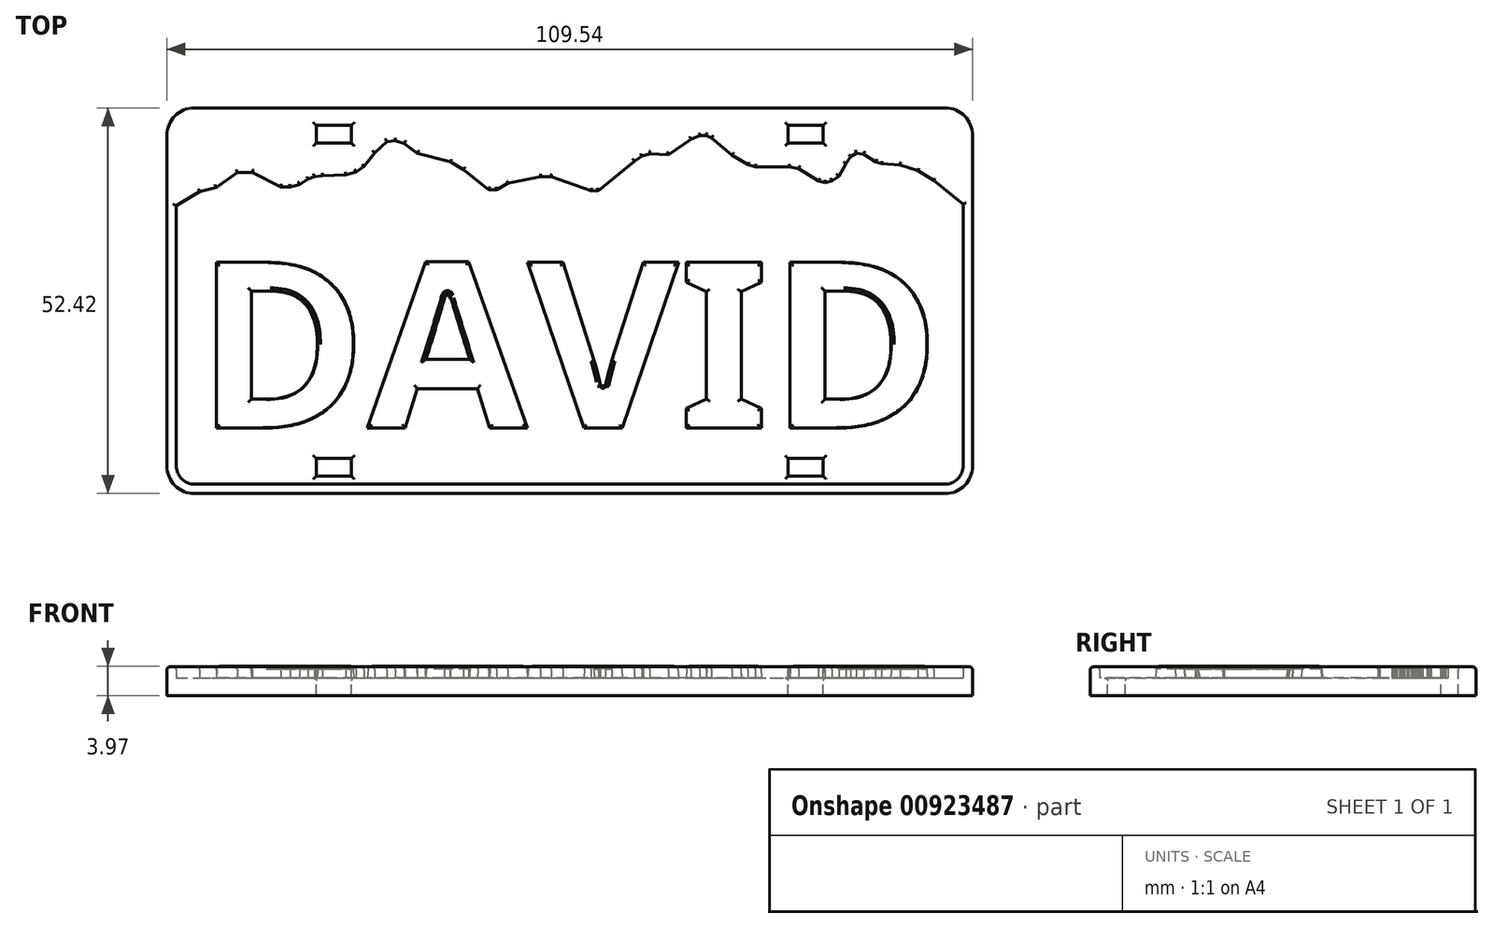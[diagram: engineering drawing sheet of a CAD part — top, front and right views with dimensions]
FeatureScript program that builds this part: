
annotation { "Feature Type Name" : "Feature", "Feature Type Description" : "" }
export const myFeature = defineFeature(function(context is Context, id is Id, definition is map)
    precondition{}
    {
        {
            var Q0;
            Q0=qCreatedBy(makeId("Top.planeOp"),FACE);
            var sketch = newSketch(context, id + "F0", { "sketchPlane" : qUnion([Q0])});
            skLineSegment(sketch, "E0", {"start": v(54.77, -22.46) * mm, "end": v(54.77, 22.46) * mm});
            skArc(sketch, "E1", {"start": v(54.77, 22.46) * mm, "mid": v(53.68, 25.11) * mm, "end": v(51.02, 26.21) * mm});
            skLineSegment(sketch, "E2", {"start": v(51.02, 26.21) * mm, "end": v(-51.02, 26.21) * mm});
            skArc(sketch, "E3", {"start": v(-51.02, 26.21) * mm, "mid": v(-53.68, 25.11) * mm, "end": v(-54.77, 22.46) * mm});
            skLineSegment(sketch, "E4", {"start": v(-54.77, 22.46) * mm, "end": v(-54.77, -22.46) * mm});
            skArc(sketch, "E5", {"start": v(-54.77, -22.46) * mm, "mid": v(-53.54, -25.24) * mm, "end": v(-50.64, -26.2) * mm});
            skLineSegment(sketch, "E6", {"start": v(-50.64, -26.2) * mm, "end": v(51.04, -26.2) * mm});
            skArc(sketch, "E7", {"start": v(51.02, -26.21) * mm, "mid": v(53.68, -25.11) * mm, "end": v(54.77, -22.46) * mm});
            skLineSegment(sketch, "E8", {"start": v(-54.77, 12.13) * mm, "end": v(-50.31, 14.84) * mm});
            skLineSegment(sketch, "E9", {"start": v(-50.31, 14.84) * mm, "end": v(-48.06, 15.4) * mm});
            skLineSegment(sketch, "E10", {"start": v(-48.06, 15.4) * mm, "end": v(-45.2, 17.44) * mm});
            skLineSegment(sketch, "E11", {"start": v(-45.2, 17.44) * mm, "end": v(-43.14, 17.44) * mm});
            skLineSegment(sketch, "E12", {"start": v(-43.14, 17.44) * mm, "end": v(-39.3, 15.5) * mm});
            skLineSegment(sketch, "E13", {"start": v(-39.3, 15.5) * mm, "end": v(-38.03, 15.49) * mm});
            skLineSegment(sketch, "E14", {"start": v(-38.03, 15.49) * mm, "end": v(-36.75, 15.8) * mm});
            skLineSegment(sketch, "E15", {"start": v(-36.75, 15.8) * mm, "end": v(-35.57, 16.54) * mm});
            skLineSegment(sketch, "E16", {"start": v(-35.57, 16.54) * mm, "end": v(-34.73, 16.88) * mm});
            skLineSegment(sketch, "E17", {"start": v(-34.73, 16.88) * mm, "end": v(-33.6, 17.01) * mm});
            skLineSegment(sketch, "E18", {"start": v(-33.6, 17.01) * mm, "end": v(-30.43, 17.11) * mm});
            skLineSegment(sketch, "E19", {"start": v(-29.05, 17.5) * mm, "end": v(-27.98, 18.27) * mm});
            skLineSegment(sketch, "E20", {"start": v(-27.98, 18.27) * mm, "end": v(-26.53, 20.14) * mm});
            skLineSegment(sketch, "E21", {"start": v(-26.53, 20.14) * mm, "end": v(-24.88, 21.63) * mm});
            skLineSegment(sketch, "E22", {"start": v(-24.88, 21.63) * mm, "end": v(-23.73, 21.77) * mm});
            skLineSegment(sketch, "E23", {"start": v(-22.5, 21.4) * mm, "end": v(-20.72, 20.04) * mm});
            skLineSegment(sketch, "E24", {"start": v(-16.23, 18.87) * mm, "end": v(-14.45, 17.85) * mm});
            skLineSegment(sketch, "E25", {"start": v(-14.45, 17.85) * mm, "end": v(-11.02, 15.1) * mm});
            skLineSegment(sketch, "E26", {"start": v(-11.02, 15.1) * mm, "end": v(-9.93, 15.1) * mm});
            skLineSegment(sketch, "E27", {"start": v(-9.93, 15.1) * mm, "end": v(-8.4, 15.96) * mm});
            skLineSegment(sketch, "E28", {"start": v(-8.4, 15.96) * mm, "end": v(-3.94, 16.85) * mm});
            skLineSegment(sketch, "E29", {"start": v(-3.94, 16.85) * mm, "end": v(-2.54, 16.85) * mm});
            skLineSegment(sketch, "E30", {"start": v(-2.54, 16.85) * mm, "end": v(2.9, 14.97) * mm});
            skLineSegment(sketch, "E31", {"start": v(2.9, 14.97) * mm, "end": v(3.92, 14.97) * mm});
            skLineSegment(sketch, "E32", {"start": v(3.92, 14.97) * mm, "end": v(8.8, 18.97) * mm});
            skLineSegment(sketch, "E33", {"start": v(8.8, 18.97) * mm, "end": v(9.82, 19.64) * mm});
            skLineSegment(sketch, "E34", {"start": v(9.82, 19.64) * mm, "end": v(10.9, 19.97) * mm});
            skLineSegment(sketch, "E35", {"start": v(10.9, 19.97) * mm, "end": v(13.43, 19.86) * mm});
            skLineSegment(sketch, "E36", {"start": v(16.5, 21.96) * mm, "end": v(17.71, 22.42) * mm});
            skLineSegment(sketch, "E37", {"start": v(17.71, 22.42) * mm, "end": v(18.56, 22.45) * mm});
            skLineSegment(sketch, "E38", {"start": v(18.56, 22.45) * mm, "end": v(19.28, 22.13) * mm});
            skLineSegment(sketch, "E39", {"start": v(19.28, 22.13) * mm, "end": v(22.05, 19.8) * mm});
            skLineSegment(sketch, "E40", {"start": v(22.05, 19.8) * mm, "end": v(24.2, 18.5) * mm});
            skLineSegment(sketch, "E41", {"start": v(24.2, 18.5) * mm, "end": v(25.23, 18.2) * mm});
            skLineSegment(sketch, "E42", {"start": v(25.23, 18.2) * mm, "end": v(29.85, 18.2) * mm});
            skLineSegment(sketch, "E43", {"start": v(29.85, 18.2) * mm, "end": v(31.13, 17.95) * mm});
            skLineSegment(sketch, "E44", {"start": v(31.13, 17.95) * mm, "end": v(33.84, 16.27) * mm});
            skLineSegment(sketch, "E45", {"start": v(33.84, 16.27) * mm, "end": v(34.73, 16.06) * mm});
            skLineSegment(sketch, "E46", {"start": v(34.73, 16.06) * mm, "end": v(35.67, 16.3) * mm});
            skLineSegment(sketch, "E47", {"start": v(35.67, 16.3) * mm, "end": v(36.58, 16.95) * mm});
            skLineSegment(sketch, "E48", {"start": v(36.58, 16.95) * mm, "end": v(37.58, 18.67) * mm});
            skLineSegment(sketch, "E49", {"start": v(38.22, 19.58) * mm, "end": v(38.96, 20.06) * mm});
            skLineSegment(sketch, "E50", {"start": v(38.96, 20.06) * mm, "end": v(39.94, 19.92) * mm});
            skLineSegment(sketch, "E51", {"start": v(41.58, 18.88) * mm, "end": v(42.4, 18.61) * mm});
            skLineSegment(sketch, "E52", {"start": v(42.4, 18.61) * mm, "end": v(44.9, 18.47) * mm});
            skLineSegment(sketch, "E53", {"start": v(44.9, 18.47) * mm, "end": v(47.31, 17.68) * mm});
            skLineSegment(sketch, "E54", {"start": v(47.31, 17.68) * mm, "end": v(49.47, 16.33) * mm});
            skLineSegment(sketch, "E55", {"start": v(49.47, 16.33) * mm, "end": v(51.88, 14.42) * mm});
            skLineSegment(sketch, "E56", {"start": v(51.88, 14.42) * mm, "end": v(53.78, 12.92) * mm});
            skLineSegment(sketch, "E57", {"start": v(53.78, 12.92) * mm, "end": v(54.77, 12.06) * mm});
            skLineSegment(sketch, "E58", {"start": v(-20.72, 20.04) * mm, "end": v(-16.23, 18.87) * mm});
            skLineSegment(sketch, "E59", {"start": v(16.5, 21.96) * mm, "end": v(13.43, 19.86) * mm});
            skLineSegment(sketch, "E60", {"start": v(-22.5, 21.4) * mm, "end": v(-23.73, 21.77) * mm});
            skLineSegment(sketch, "E61", {"start": v(-29.05, 17.5) * mm, "end": v(-30.43, 17.11) * mm});
            skLineSegment(sketch, "E62", {"start": v(37.58, 18.67) * mm, "end": v(38.22, 19.58) * mm});
            skLineSegment(sketch, "E63", {"start": v(41.58, 18.88) * mm, "end": v(39.94, 19.92) * mm});
            skSolve(sketch);
        }
        {
            var Q0;
            Q0=qCreatedBy(makeId("Top.planeOp"),FACE);
            var sketch = newSketch(context, id + "F1", { "sketchPlane" : qUnion([Q0])});
            skLineSegment(sketch, "E64", {"start": v(54.77, -22.46) * mm, "end": v(54.77, 22.46) * mm});
            skArc(sketch, "E65", {"start": v(54.77, 22.46) * mm, "mid": v(53.68, 25.11) * mm, "end": v(51.02, 26.21) * mm});
            skLineSegment(sketch, "E66", {"start": v(51.02, 26.21) * mm, "end": v(-51.02, 26.21) * mm});
            skArc(sketch, "E67", {"start": v(-51.02, 26.21) * mm, "mid": v(-53.68, 25.11) * mm, "end": v(-54.77, 22.46) * mm});
            skLineSegment(sketch, "E68", {"start": v(-54.77, 22.46) * mm, "end": v(-54.77, -22.46) * mm});
            skArc(sketch, "E69", {"start": v(-54.77, -22.46) * mm, "mid": v(-53.68, -25.11) * mm, "end": v(-51.02, -26.21) * mm});
            skLineSegment(sketch, "E70", {"start": v(-51.02, -26.21) * mm, "end": v(51.02, -26.21) * mm});
            skArc(sketch, "E71", {"start": v(51.02, -26.21) * mm, "mid": v(53.68, -25.11) * mm, "end": v(54.77, -22.46) * mm});
            skLineSegment(sketch, "E72.0", {"start": v(50.96, 24.94) * mm, "end": v(-50.96, 24.94) * mm, "construction": true});
            skLineSegment(sketch, "E72.1", {"start": v(53.5, -22.4) * mm, "end": v(53.5, 22.4) * mm, "construction": true});
            skLineSegment(sketch, "E72.2", {"start": v(-50.96, -24.94) * mm, "end": v(50.96, -24.94) * mm, "construction": true});
            skLineSegment(sketch, "E72.3", {"start": v(-53.5, 22.4) * mm, "end": v(-53.5, -22.4) * mm, "construction": true});
            skPoint(sketch, "E73.visualSharp", {"position": v(-53.5, 24.94) * mm});
            skArc(sketch, "E73.filletArc", {"start": v(-50.96, 24.94) * mm, "mid": v(-52.76, 24.2) * mm, "end": v(-53.5, 22.4) * mm, "construction": true});
            skPoint(sketch, "E74.visualSharp", {"position": v(-53.5, -24.94) * mm});
            skArc(sketch, "E74.filletArc", {"start": v(-53.5, -22.4) * mm, "mid": v(-52.76, -24.2) * mm, "end": v(-50.96, -24.94) * mm, "construction": true});
            skPoint(sketch, "E75.visualSharp", {"position": v(53.5, -24.94) * mm});
            skArc(sketch, "E75.filletArc", {"start": v(50.96, -24.94) * mm, "mid": v(52.76, -24.2) * mm, "end": v(53.5, -22.4) * mm, "construction": true});
            skPoint(sketch, "E76.visualSharp", {"position": v(53.5, 24.94) * mm});
            skArc(sketch, "E76.filletArc", {"start": v(53.5, 22.4) * mm, "mid": v(52.76, 24.2) * mm, "end": v(50.96, 24.94) * mm, "construction": true});
            skSolve(sketch);
        }
        {
            var Q0;
            {var subQ3=sQuery(id+"F0.wireOp",EDGE,"E1");Q0=makeQuery(id+"F0.imprint","IMPRINT",FACE,{"disambiguationData":[TD([[makeQuery(id+"F0.imprint","IMPRINT",EDGE,{"derivedFrom":subQ3}),1.0]])]});}
            extrude(context, id + "F2", {"entities" : qUnion([Q0]), "depth" : 1.52 * mm, "offsetDistance" : 25.4 * mm});
        }
        {
            var Q0;
            Q0=qSketchRegion(id+"F1",true);
            extrude(context, id + "F3", {"entities" : qUnion([Q0]), "operationType" : NewBodyOperationType.ADD, "oppositeDirection" : true, "depth" : 2.38 * mm, "offsetDistance" : 25.4 * mm});
        }
        {
            var Q0;
            {var subQ58=sQuery(id+"F0.wireOp",EDGE,"E0");var subQ59=sQuery(id+"F1.wireOp",EDGE,"E64");var subQ60=sQuery(id+"F1.wireOp",EDGE,"E65");var subQ61=sQuery(id+"F1.wireOp",EDGE,"E68");var subQ62=sQuery(id+"F1.wireOp",EDGE,"E69");var subQ63=sQuery(id+"F1.wireOp",EDGE,"E70");var subQ64=sQuery(id+"F1.wireOp",EDGE,"E71");Q0=makeQuery(id+"F3.boolean.opBoolean","SPLIT",FACE,{"disambiguationData":[TD([makeQuery(id+"F2.opExtrude","SWEPT_FACE",FACE,{"disambiguationData":[OSD([subQ58])]})])],"derivedFrom":makeQuery(id+"F3.opExtrude","CAP_FACE",FACE,{"disambiguationData":[OSD([subQ59,subQ60,sQuery(id+"F1.wireOp",EDGE,"E66"),sQuery(id+"F1.wireOp",EDGE,"E67"),subQ61,subQ62,subQ63,subQ64])],"isStart":true})});}
            var sketch = newSketch(context, id + "F4", { "sketchPlane" : qUnion([Q0])});
            skLineSegment(sketch, "E77", {"start": v(54.77, -22.46) * mm, "end": v(54.77, 12.06) * mm});
            skLineSegment(sketch, "E78", {"start": v(-54.77, 12.13) * mm, "end": v(-54.77, -22.46) * mm});
            skArc(sketch, "E79", {"start": v(-54.77, -22.46) * mm, "mid": v(-53.68, -25.11) * mm, "end": v(-51.02, -26.21) * mm});
            skLineSegment(sketch, "E80", {"start": v(-51.02, -26.21) * mm, "end": v(51.02, -26.21) * mm});
            skArc(sketch, "E81", {"start": v(51.02, -26.21) * mm, "mid": v(53.68, -25.11) * mm, "end": v(54.77, -22.46) * mm});
            skLineSegment(sketch, "E82.1", {"start": v(53.5, -22.4) * mm, "end": v(53.5, 13.14) * mm});
            skLineSegment(sketch, "E82.2", {"start": v(-50.96, -24.94) * mm, "end": v(50.96, -24.94) * mm});
            skLineSegment(sketch, "E82.3", {"start": v(-53.5, 12.9) * mm, "end": v(-53.5, -22.4) * mm});
            skPoint(sketch, "E83.visualSharp", {"position": v(-53.5, 24.94) * mm});
            skPoint(sketch, "E84.visualSharp", {"position": v(-53.5, -24.94) * mm});
            skArc(sketch, "E84.filletArc", {"start": v(-53.5, -22.4) * mm, "mid": v(-52.76, -24.2) * mm, "end": v(-50.96, -24.94) * mm});
            skPoint(sketch, "E85.visualSharp", {"position": v(53.5, -24.94) * mm});
            skArc(sketch, "E85.filletArc", {"start": v(50.96, -24.94) * mm, "mid": v(52.76, -24.2) * mm, "end": v(53.5, -22.4) * mm});
            skPoint(sketch, "E86.visualSharp", {"position": v(53.5, 24.94) * mm});
            skLineSegment(sketch, "E87", {"start": v(-54.77, 12.13) * mm, "end": v(-53.5, 12.9) * mm});
            skLineSegment(sketch, "E88", {"start": v(53.5, 13.14) * mm, "end": v(53.78, 12.92) * mm});
            skLineSegment(sketch, "E89", {"start": v(53.78, 12.92) * mm, "end": v(54.77, 12.06) * mm});
            skSolve(sketch);
        }
        {
            var Q0;
            Q0=qSketchRegion(id+"F4",true);
            extrude(context, id + "F5", {"entities" : qUnion([Q0]), "operationType" : NewBodyOperationType.ADD, "depth" : 1.52 * mm, "offsetDistance" : 25.4 * mm});
        }
        {
            var Q0;
            Q0=makeQuery(id+"F5.boolean.opBoolean","MERGE",FACE,{"derivedFrom":[makeQuery(id+"F2.opExtrude","CAP_FACE",FACE,{"disambiguationData":[OSD([sQuery(id+"F0.wireOp",EDGE,"E0"),sQuery(id+"F0.wireOp",EDGE,"E1"),sQuery(id+"F0.wireOp",EDGE,"E2"),sQuery(id+"F0.wireOp",EDGE,"E3"),sQuery(id+"F0.wireOp",EDGE,"E4"),sQuery(id+"F0.wireOp",EDGE,"E8"),sQuery(id+"F0.wireOp",EDGE,"E9"),sQuery(id+"F0.wireOp",EDGE,"E10"),sQuery(id+"F0.wireOp",EDGE,"E11"),sQuery(id+"F0.wireOp",EDGE,"E12"),sQuery(id+"F0.wireOp",EDGE,"E13"),sQuery(id+"F0.wireOp",EDGE,"E14"),sQuery(id+"F0.wireOp",EDGE,"E15"),sQuery(id+"F0.wireOp",EDGE,"E16"),sQuery(id+"F0.wireOp",EDGE,"E17"),sQuery(id+"F0.wireOp",EDGE,"E18"),sQuery(id+"F0.wireOp",EDGE,"7b9f405e-0691-426e-9c9e-a5372cf0836a"),sQuery(id+"F0.wireOp",EDGE,"E19"),sQuery(id+"F0.wireOp",EDGE,"E20"),sQuery(id+"F0.wireOp",EDGE,"E21"),sQuery(id+"F0.wireOp",EDGE,"E22"),sQuery(id+"F0.wireOp",EDGE,"b3dec5b1-662c-4d50-a13c-af7b7760114a"),sQuery(id+"F0.wireOp",EDGE,"E23"),sQuery(id+"F0.wireOp",EDGE,"4d9ee76e-0833-4cdc-b1a8-2d4ce76e6521"),sQuery(id+"F0.wireOp",EDGE,"E24"),sQuery(id+"F0.wireOp",EDGE,"E25"),sQuery(id+"F0.wireOp",EDGE,"E26"),sQuery(id+"F0.wireOp",EDGE,"E27"),sQuery(id+"F0.wireOp",EDGE,"E28"),sQuery(id+"F0.wireOp",EDGE,"E29"),sQuery(id+"F0.wireOp",EDGE,"E30"),sQuery(id+"F0.wireOp",EDGE,"E31"),sQuery(id+"F0.wireOp",EDGE,"E32"),sQuery(id+"F0.wireOp",EDGE,"E33"),sQuery(id+"F0.wireOp",EDGE,"E34"),sQuery(id+"F0.wireOp",EDGE,"E35"),sQuery(id+"F0.wireOp",EDGE,"55551997-bb9e-4b94-90c5-def3cb147476"),sQuery(id+"F0.wireOp",EDGE,"E36"),sQuery(id+"F0.wireOp",EDGE,"E37"),sQuery(id+"F0.wireOp",EDGE,"E38"),sQuery(id+"F0.wireOp",EDGE,"E39"),sQuery(id+"F0.wireOp",EDGE,"E40"),sQuery(id+"F0.wireOp",EDGE,"E41"),sQuery(id+"F0.wireOp",EDGE,"E42"),sQuery(id+"F0.wireOp",EDGE,"E43"),sQuery(id+"F0.wireOp",EDGE,"E44"),sQuery(id+"F0.wireOp",EDGE,"E45"),sQuery(id+"F0.wireOp",EDGE,"E46"),sQuery(id+"F0.wireOp",EDGE,"E47"),sQuery(id+"F0.wireOp",EDGE,"E48"),sQuery(id+"F0.wireOp",EDGE,"513b7cbe-d979-4e22-b277-f3c42ccdbda1"),sQuery(id+"F0.wireOp",EDGE,"E49"),sQuery(id+"F0.wireOp",EDGE,"E50"),sQuery(id+"F0.wireOp",EDGE,"0d842e13-672c-40e3-aae4-28923e78d4e0"),sQuery(id+"F0.wireOp",EDGE,"E51"),sQuery(id+"F0.wireOp",EDGE,"E52"),sQuery(id+"F0.wireOp",EDGE,"E53"),sQuery(id+"F0.wireOp",EDGE,"E54"),sQuery(id+"F0.wireOp",EDGE,"E55"),sQuery(id+"F0.wireOp",EDGE,"E56"),sQuery(id+"F0.wireOp",EDGE,"E57")])],"isStart":false}),makeQuery(id+"F5.opExtrude","CAP_FACE",FACE,{"disambiguationData":[OSD([sQuery(id+"F4.wireOp",EDGE,"E77"),sQuery(id+"F4.wireOp",EDGE,"E78"),sQuery(id+"F4.wireOp",EDGE,"E79"),sQuery(id+"F4.wireOp",EDGE,"E80"),sQuery(id+"F4.wireOp",EDGE,"E81"),sQuery(id+"F4.wireOp",EDGE,"E82.1"),sQuery(id+"F4.wireOp",EDGE,"E82.2"),sQuery(id+"F4.wireOp",EDGE,"E82.3"),sQuery(id+"F4.wireOp",EDGE,"E84.filletArc"),sQuery(id+"F4.wireOp",EDGE,"E85.filletArc"),sQuery(id+"F4.wireOp",EDGE,"E87"),sQuery(id+"F4.wireOp",EDGE,"E88"),sQuery(id+"F4.wireOp",EDGE,"E89")])],"isStart":false})]});
            var sketch = newSketch(context, id + "F6", { "sketchPlane" : qUnion([Q0])});
            skLineSegment(sketch, "E90.bottom", {"start": v(-34.45, 23.83) * mm, "end": v(-29.7, 23.83) * mm});
            skLineSegment(sketch, "E90.top", {"start": v(-34.45, 21.45) * mm, "end": v(-29.7, 21.45) * mm});
            skLineSegment(sketch, "E90.left", {"start": v(-34.45, 23.83) * mm, "end": v(-34.45, 21.45) * mm});
            skLineSegment(sketch, "E90.right", {"start": v(-29.7, 23.83) * mm, "end": v(-29.7, 21.45) * mm});
            skLineSegment(sketch, "E91", {"start": v(0, 26.21) * mm, "end": v(0, -26.21) * mm, "construction": true});
            skLineSegment(sketch, "E92.MirrorCS", {"start": v(34.45, 23.83) * mm, "end": v(34.45, 21.45) * mm});
            skLineSegment(sketch, "E93.MirrorCS", {"start": v(29.7, 23.83) * mm, "end": v(29.7, 21.45) * mm});
            skLineSegment(sketch, "E94.MirrorCS", {"start": v(34.45, 21.45) * mm, "end": v(29.7, 21.45) * mm});
            skLineSegment(sketch, "E95.MirrorCS", {"start": v(34.45, 23.83) * mm, "end": v(29.7, 23.83) * mm});
            skLineSegment(sketch, "E96", {"start": v(0, 0) * mm, "end": v(-59.23, 0) * mm, "construction": true});
            skLineSegment(sketch, "E97", {"start": v(0, 0) * mm, "end": v(56.47, 0) * mm, "construction": true});
            skLineSegment(sketch, "E98.MirrorCS", {"start": v(-34.45, -23.83) * mm, "end": v(-29.7, -23.83) * mm});
            skLineSegment(sketch, "E99.MirrorCS", {"start": v(-34.45, -23.83) * mm, "end": v(-34.45, -21.45) * mm});
            skLineSegment(sketch, "E100.MirrorCS", {"start": v(-34.45, -21.45) * mm, "end": v(-29.7, -21.45) * mm});
            skLineSegment(sketch, "E101.MirrorCS", {"start": v(-29.7, -23.83) * mm, "end": v(-29.7, -21.45) * mm});
            skLineSegment(sketch, "E102.MirrorCS", {"start": v(29.7, -23.83) * mm, "end": v(29.7, -21.45) * mm});
            skLineSegment(sketch, "E103.MirrorCS", {"start": v(34.45, -23.83) * mm, "end": v(29.7, -23.83) * mm});
            skLineSegment(sketch, "E104.MirrorCS", {"start": v(34.45, -23.83) * mm, "end": v(34.45, -21.45) * mm});
            skLineSegment(sketch, "E105.MirrorCS", {"start": v(34.45, -21.45) * mm, "end": v(29.7, -21.45) * mm});
            skSolve(sketch);
        }
        {
            var Q0;
            Q0=qSketchRegion(id+"F6",true);
            extrude(context, id + "F7", {"entities" : qUnion([Q0]), "operationType" : NewBodyOperationType.REMOVE, "endBound" : BoundingType.THROUGH_ALL, "oppositeDirection" : true, "depth" : 25.4 * mm, "offsetDistance" : 25.4 * mm});
        }
        {
            var Q0;
            Q0=makeQuery(id+"F3.opExtrude","CAP_FACE",FACE,{"disambiguationData":[OSD([sQuery(id+"F1.wireOp",EDGE,"E64"),sQuery(id+"F1.wireOp",EDGE,"E65"),sQuery(id+"F1.wireOp",EDGE,"E66"),sQuery(id+"F1.wireOp",EDGE,"E67"),sQuery(id+"F1.wireOp",EDGE,"E68"),sQuery(id+"F1.wireOp",EDGE,"E69"),sQuery(id+"F1.wireOp",EDGE,"E70"),sQuery(id+"F1.wireOp",EDGE,"E71")])],"isStart":true});
            var sketch = newSketch(context, id + "F8", { "sketchPlane" : qUnion([Q0])});
            skText(sketch, "E106", { "text": "DAVID", "fontName": "NotoSans-Bold.ttf"});
            const initialGuessF8  = {"E106": [-0.0509, -0.01732, 1, 0, 0.02274]};
            skSetInitialGuess(sketch, initialGuessF8);
            skSolve(sketch);
        }
        {
            var Q0;
            Q0=qSketchRegion(id+"F8",true);
            extrude(context, id + "F9", {"entities" : qUnion([Q0]), "operationType" : NewBodyOperationType.ADD, "depth" : 1.59 * mm, "offsetDistance" : 25.4 * mm, "hasDraft" : true, "draftAngle" : 3 * degree, "draftPullDirection" : true});
        }
        {
            var Q0;
            Q0=makeQuery(id+"F5.boolean.opBoolean","MERGE",FACE,{"derivedFrom":[makeQuery(id+"F2.opExtrude","CAP_FACE",FACE,{"disambiguationData":[OSD([sQuery(id+"F0.wireOp",EDGE,"E0"),sQuery(id+"F0.wireOp",EDGE,"E1"),sQuery(id+"F0.wireOp",EDGE,"E2"),sQuery(id+"F0.wireOp",EDGE,"E3"),sQuery(id+"F0.wireOp",EDGE,"E4"),sQuery(id+"F0.wireOp",EDGE,"E8"),sQuery(id+"F0.wireOp",EDGE,"E9"),sQuery(id+"F0.wireOp",EDGE,"E10"),sQuery(id+"F0.wireOp",EDGE,"E11"),sQuery(id+"F0.wireOp",EDGE,"E12"),sQuery(id+"F0.wireOp",EDGE,"E13"),sQuery(id+"F0.wireOp",EDGE,"E14"),sQuery(id+"F0.wireOp",EDGE,"E15"),sQuery(id+"F0.wireOp",EDGE,"E16"),sQuery(id+"F0.wireOp",EDGE,"E17"),sQuery(id+"F0.wireOp",EDGE,"E18"),sQuery(id+"F0.wireOp",EDGE,"7b9f405e-0691-426e-9c9e-a5372cf0836a"),sQuery(id+"F0.wireOp",EDGE,"E19"),sQuery(id+"F0.wireOp",EDGE,"E20"),sQuery(id+"F0.wireOp",EDGE,"E21"),sQuery(id+"F0.wireOp",EDGE,"E22"),sQuery(id+"F0.wireOp",EDGE,"b3dec5b1-662c-4d50-a13c-af7b7760114a"),sQuery(id+"F0.wireOp",EDGE,"E23"),sQuery(id+"F0.wireOp",EDGE,"4d9ee76e-0833-4cdc-b1a8-2d4ce76e6521"),sQuery(id+"F0.wireOp",EDGE,"E24"),sQuery(id+"F0.wireOp",EDGE,"E25"),sQuery(id+"F0.wireOp",EDGE,"E26"),sQuery(id+"F0.wireOp",EDGE,"E27"),sQuery(id+"F0.wireOp",EDGE,"E28"),sQuery(id+"F0.wireOp",EDGE,"E29"),sQuery(id+"F0.wireOp",EDGE,"E30"),sQuery(id+"F0.wireOp",EDGE,"E31"),sQuery(id+"F0.wireOp",EDGE,"E32"),sQuery(id+"F0.wireOp",EDGE,"E33"),sQuery(id+"F0.wireOp",EDGE,"E34"),sQuery(id+"F0.wireOp",EDGE,"E35"),sQuery(id+"F0.wireOp",EDGE,"55551997-bb9e-4b94-90c5-def3cb147476"),sQuery(id+"F0.wireOp",EDGE,"E36"),sQuery(id+"F0.wireOp",EDGE,"E37"),sQuery(id+"F0.wireOp",EDGE,"E38"),sQuery(id+"F0.wireOp",EDGE,"E39"),sQuery(id+"F0.wireOp",EDGE,"E40"),sQuery(id+"F0.wireOp",EDGE,"E41"),sQuery(id+"F0.wireOp",EDGE,"E42"),sQuery(id+"F0.wireOp",EDGE,"E43"),sQuery(id+"F0.wireOp",EDGE,"E44"),sQuery(id+"F0.wireOp",EDGE,"E45"),sQuery(id+"F0.wireOp",EDGE,"E46"),sQuery(id+"F0.wireOp",EDGE,"E47"),sQuery(id+"F0.wireOp",EDGE,"E48"),sQuery(id+"F0.wireOp",EDGE,"513b7cbe-d979-4e22-b277-f3c42ccdbda1"),sQuery(id+"F0.wireOp",EDGE,"E49"),sQuery(id+"F0.wireOp",EDGE,"E50"),sQuery(id+"F0.wireOp",EDGE,"0d842e13-672c-40e3-aae4-28923e78d4e0"),sQuery(id+"F0.wireOp",EDGE,"E51"),sQuery(id+"F0.wireOp",EDGE,"E52"),sQuery(id+"F0.wireOp",EDGE,"E53"),sQuery(id+"F0.wireOp",EDGE,"E54"),sQuery(id+"F0.wireOp",EDGE,"E55"),sQuery(id+"F0.wireOp",EDGE,"E56"),sQuery(id+"F0.wireOp",EDGE,"E57")])],"isStart":false}),makeQuery(id+"F5.opExtrude","CAP_FACE",FACE,{"disambiguationData":[OSD([sQuery(id+"F4.wireOp",EDGE,"E77"),sQuery(id+"F4.wireOp",EDGE,"E78"),sQuery(id+"F4.wireOp",EDGE,"E79"),sQuery(id+"F4.wireOp",EDGE,"E80"),sQuery(id+"F4.wireOp",EDGE,"E81"),sQuery(id+"F4.wireOp",EDGE,"E82.1"),sQuery(id+"F4.wireOp",EDGE,"E82.2"),sQuery(id+"F4.wireOp",EDGE,"E82.3"),sQuery(id+"F4.wireOp",EDGE,"E84.filletArc"),sQuery(id+"F4.wireOp",EDGE,"E85.filletArc"),sQuery(id+"F4.wireOp",EDGE,"E87"),sQuery(id+"F4.wireOp",EDGE,"E88"),sQuery(id+"F4.wireOp",EDGE,"E89")])],"isStart":false})]});
            var Q1;
            {var subQ0=sQuery(id+"F1.wireOp",EDGE,"E64");var subQ1=sQuery(id+"F1.wireOp",EDGE,"E68");var subQ2=sQuery(id+"F1.wireOp",EDGE,"E69");var subQ3=sQuery(id+"F1.wireOp",EDGE,"E70");var subQ4=sQuery(id+"F1.wireOp",EDGE,"E71");Q1=makeQuery(id+"F7.boolean.opBoolean","INTERSECT",EDGE,{"derivedFrom":[makeQuery(id+"F3.boolean.opBoolean","SPLIT",FACE,{"disambiguationData":[TD([makeQuery(id+"F2.opExtrude","SWEPT_FACE",FACE,{"disambiguationData":[OSD([sQuery(id+"F0.wireOp",EDGE,"E0")])]})])],"derivedFrom":makeQuery(id+"F3.opExtrude","CAP_FACE",FACE,{"disambiguationData":[OSD([subQ0,sQuery(id+"F1.wireOp",EDGE,"E65"),sQuery(id+"F1.wireOp",EDGE,"E66"),sQuery(id+"F1.wireOp",EDGE,"E67"),subQ1,subQ2,subQ3,subQ4])],"isStart":true})}),makeQuery(id+"F7.opExtrude","SWEPT_FACE",FACE,{"disambiguationData":[OSD([sQuery(id+"F6.wireOp",EDGE,"E100.MirrorCS")])]})]});}
            var Q2;
            {var subQ0=sQuery(id+"F1.wireOp",EDGE,"E64");var subQ1=sQuery(id+"F1.wireOp",EDGE,"E68");var subQ2=sQuery(id+"F1.wireOp",EDGE,"E69");var subQ3=sQuery(id+"F1.wireOp",EDGE,"E70");var subQ4=sQuery(id+"F1.wireOp",EDGE,"E71");Q2=makeQuery(id+"F7.boolean.opBoolean","INTERSECT",EDGE,{"derivedFrom":[makeQuery(id+"F3.boolean.opBoolean","SPLIT",FACE,{"disambiguationData":[TD([makeQuery(id+"F2.opExtrude","SWEPT_FACE",FACE,{"disambiguationData":[OSD([sQuery(id+"F0.wireOp",EDGE,"E0")])]})])],"derivedFrom":makeQuery(id+"F3.opExtrude","CAP_FACE",FACE,{"disambiguationData":[OSD([subQ0,sQuery(id+"F1.wireOp",EDGE,"E65"),sQuery(id+"F1.wireOp",EDGE,"E66"),sQuery(id+"F1.wireOp",EDGE,"E67"),subQ1,subQ2,subQ3,subQ4])],"isStart":true})}),makeQuery(id+"F7.opExtrude","SWEPT_FACE",FACE,{"disambiguationData":[OSD([sQuery(id+"F6.wireOp",EDGE,"E99.MirrorCS")])]})]});}
            var Q3;
            {var subQ0=sQuery(id+"F1.wireOp",EDGE,"E64");var subQ1=sQuery(id+"F1.wireOp",EDGE,"E68");var subQ2=sQuery(id+"F1.wireOp",EDGE,"E69");var subQ3=sQuery(id+"F1.wireOp",EDGE,"E70");var subQ4=sQuery(id+"F1.wireOp",EDGE,"E71");Q3=makeQuery(id+"F7.boolean.opBoolean","INTERSECT",EDGE,{"derivedFrom":[makeQuery(id+"F3.boolean.opBoolean","SPLIT",FACE,{"disambiguationData":[TD([makeQuery(id+"F2.opExtrude","SWEPT_FACE",FACE,{"disambiguationData":[OSD([sQuery(id+"F0.wireOp",EDGE,"E0")])]})])],"derivedFrom":makeQuery(id+"F3.opExtrude","CAP_FACE",FACE,{"disambiguationData":[OSD([subQ0,sQuery(id+"F1.wireOp",EDGE,"E65"),sQuery(id+"F1.wireOp",EDGE,"E66"),sQuery(id+"F1.wireOp",EDGE,"E67"),subQ1,subQ2,subQ3,subQ4])],"isStart":true})}),makeQuery(id+"F7.opExtrude","SWEPT_FACE",FACE,{"disambiguationData":[OSD([sQuery(id+"F6.wireOp",EDGE,"E98.MirrorCS")])]})]});}
            var Q4;
            {var subQ0=sQuery(id+"F1.wireOp",EDGE,"E64");var subQ1=sQuery(id+"F1.wireOp",EDGE,"E68");var subQ2=sQuery(id+"F1.wireOp",EDGE,"E69");var subQ3=sQuery(id+"F1.wireOp",EDGE,"E70");var subQ4=sQuery(id+"F1.wireOp",EDGE,"E71");Q4=makeQuery(id+"F7.boolean.opBoolean","INTERSECT",EDGE,{"derivedFrom":[makeQuery(id+"F3.boolean.opBoolean","SPLIT",FACE,{"disambiguationData":[TD([makeQuery(id+"F2.opExtrude","SWEPT_FACE",FACE,{"disambiguationData":[OSD([sQuery(id+"F0.wireOp",EDGE,"E0")])]})])],"derivedFrom":makeQuery(id+"F3.opExtrude","CAP_FACE",FACE,{"disambiguationData":[OSD([subQ0,sQuery(id+"F1.wireOp",EDGE,"E65"),sQuery(id+"F1.wireOp",EDGE,"E66"),sQuery(id+"F1.wireOp",EDGE,"E67"),subQ1,subQ2,subQ3,subQ4])],"isStart":true})}),makeQuery(id+"F7.opExtrude","SWEPT_FACE",FACE,{"disambiguationData":[OSD([sQuery(id+"F6.wireOp",EDGE,"E101.MirrorCS")])]})]});}
            var Q5;
            {var subQ0=sQuery(id+"F1.wireOp",EDGE,"E64");var subQ1=sQuery(id+"F1.wireOp",EDGE,"E68");var subQ2=sQuery(id+"F1.wireOp",EDGE,"E69");var subQ3=sQuery(id+"F1.wireOp",EDGE,"E70");var subQ4=sQuery(id+"F1.wireOp",EDGE,"E71");Q5=makeQuery(id+"F7.boolean.opBoolean","INTERSECT",EDGE,{"derivedFrom":[makeQuery(id+"F3.boolean.opBoolean","SPLIT",FACE,{"disambiguationData":[TD([makeQuery(id+"F2.opExtrude","SWEPT_FACE",FACE,{"disambiguationData":[OSD([sQuery(id+"F0.wireOp",EDGE,"E0")])]})])],"derivedFrom":makeQuery(id+"F3.opExtrude","CAP_FACE",FACE,{"disambiguationData":[OSD([subQ0,sQuery(id+"F1.wireOp",EDGE,"E65"),sQuery(id+"F1.wireOp",EDGE,"E66"),sQuery(id+"F1.wireOp",EDGE,"E67"),subQ1,subQ2,subQ3,subQ4])],"isStart":true})}),makeQuery(id+"F7.opExtrude","SWEPT_FACE",FACE,{"disambiguationData":[OSD([sQuery(id+"F6.wireOp",EDGE,"E102.MirrorCS")])]})]});}
            var Q6;
            {var subQ0=sQuery(id+"F1.wireOp",EDGE,"E64");var subQ1=sQuery(id+"F1.wireOp",EDGE,"E68");var subQ2=sQuery(id+"F1.wireOp",EDGE,"E69");var subQ3=sQuery(id+"F1.wireOp",EDGE,"E70");var subQ4=sQuery(id+"F1.wireOp",EDGE,"E71");Q6=makeQuery(id+"F7.boolean.opBoolean","INTERSECT",EDGE,{"derivedFrom":[makeQuery(id+"F3.boolean.opBoolean","SPLIT",FACE,{"disambiguationData":[TD([makeQuery(id+"F2.opExtrude","SWEPT_FACE",FACE,{"disambiguationData":[OSD([sQuery(id+"F0.wireOp",EDGE,"E0")])]})])],"derivedFrom":makeQuery(id+"F3.opExtrude","CAP_FACE",FACE,{"disambiguationData":[OSD([subQ0,sQuery(id+"F1.wireOp",EDGE,"E65"),sQuery(id+"F1.wireOp",EDGE,"E66"),sQuery(id+"F1.wireOp",EDGE,"E67"),subQ1,subQ2,subQ3,subQ4])],"isStart":true})}),makeQuery(id+"F7.opExtrude","SWEPT_FACE",FACE,{"disambiguationData":[OSD([sQuery(id+"F6.wireOp",EDGE,"E105.MirrorCS")])]})]});}
            var Q7;
            {var subQ0=sQuery(id+"F1.wireOp",EDGE,"E64");var subQ1=sQuery(id+"F1.wireOp",EDGE,"E68");var subQ2=sQuery(id+"F1.wireOp",EDGE,"E69");var subQ3=sQuery(id+"F1.wireOp",EDGE,"E70");var subQ4=sQuery(id+"F1.wireOp",EDGE,"E71");Q7=makeQuery(id+"F7.boolean.opBoolean","INTERSECT",EDGE,{"derivedFrom":[makeQuery(id+"F3.boolean.opBoolean","SPLIT",FACE,{"disambiguationData":[TD([makeQuery(id+"F2.opExtrude","SWEPT_FACE",FACE,{"disambiguationData":[OSD([sQuery(id+"F0.wireOp",EDGE,"E0")])]})])],"derivedFrom":makeQuery(id+"F3.opExtrude","CAP_FACE",FACE,{"disambiguationData":[OSD([subQ0,sQuery(id+"F1.wireOp",EDGE,"E65"),sQuery(id+"F1.wireOp",EDGE,"E66"),sQuery(id+"F1.wireOp",EDGE,"E67"),subQ1,subQ2,subQ3,subQ4])],"isStart":true})}),makeQuery(id+"F7.opExtrude","SWEPT_FACE",FACE,{"disambiguationData":[OSD([sQuery(id+"F6.wireOp",EDGE,"E104.MirrorCS")])]})]});}
            var Q8;
            {var subQ0=sQuery(id+"F1.wireOp",EDGE,"E64");var subQ1=sQuery(id+"F1.wireOp",EDGE,"E68");var subQ2=sQuery(id+"F1.wireOp",EDGE,"E69");var subQ3=sQuery(id+"F1.wireOp",EDGE,"E70");var subQ4=sQuery(id+"F1.wireOp",EDGE,"E71");Q8=makeQuery(id+"F7.boolean.opBoolean","INTERSECT",EDGE,{"derivedFrom":[makeQuery(id+"F3.boolean.opBoolean","SPLIT",FACE,{"disambiguationData":[TD([makeQuery(id+"F2.opExtrude","SWEPT_FACE",FACE,{"disambiguationData":[OSD([sQuery(id+"F0.wireOp",EDGE,"E0")])]})])],"derivedFrom":makeQuery(id+"F3.opExtrude","CAP_FACE",FACE,{"disambiguationData":[OSD([subQ0,sQuery(id+"F1.wireOp",EDGE,"E65"),sQuery(id+"F1.wireOp",EDGE,"E66"),sQuery(id+"F1.wireOp",EDGE,"E67"),subQ1,subQ2,subQ3,subQ4])],"isStart":true})}),makeQuery(id+"F7.opExtrude","SWEPT_FACE",FACE,{"disambiguationData":[OSD([sQuery(id+"F6.wireOp",EDGE,"E103.MirrorCS")])]})]});}
            var Q9;
            Q9=makeQuery(id+"F9.opExtrude","CAP_FACE",FACE,{"disambiguationData":[OSD([sQuery(id+"F8.wireOp",EDGE,"E106.sketch_text.stroke-0"),sQuery(id+"F8.wireOp",EDGE,"E106.sketch_text.stroke-1"),sQuery(id+"F8.wireOp",EDGE,"E106.sketch_text.stroke-2"),sQuery(id+"F8.wireOp",EDGE,"E106.sketch_text.stroke-3"),sQuery(id+"F8.wireOp",EDGE,"E106.sketch_text.stroke-4"),sQuery(id+"F8.wireOp",EDGE,"E106.sketch_text.stroke-5"),sQuery(id+"F8.wireOp",EDGE,"E106.sketch_text.stroke-6"),sQuery(id+"F8.wireOp",EDGE,"E106.sketch_text.stroke-7"),sQuery(id+"F8.wireOp",EDGE,"E106.sketch_text.stroke-8"),sQuery(id+"F8.wireOp",EDGE,"E106.sketch_text.stroke-9"),sQuery(id+"F8.wireOp",EDGE,"E106.sketch_text.stroke-10"),sQuery(id+"F8.wireOp",EDGE,"E106.sketch_text.stroke-11")])],"isStart":false});
            var Q10;
            Q10=makeQuery(id+"F9.opExtrude","CAP_FACE",FACE,{"disambiguationData":[OSD([sQuery(id+"F8.wireOp",EDGE,"E106.sketch_text.stroke-12"),sQuery(id+"F8.wireOp",EDGE,"E106.sketch_text.stroke-13"),sQuery(id+"F8.wireOp",EDGE,"E106.sketch_text.stroke-14"),sQuery(id+"F8.wireOp",EDGE,"E106.sketch_text.stroke-15"),sQuery(id+"F8.wireOp",EDGE,"E106.sketch_text.stroke-16"),sQuery(id+"F8.wireOp",EDGE,"E106.sketch_text.stroke-17"),sQuery(id+"F8.wireOp",EDGE,"E106.sketch_text.stroke-18"),sQuery(id+"F8.wireOp",EDGE,"E106.sketch_text.stroke-19"),sQuery(id+"F8.wireOp",EDGE,"E106.sketch_text.stroke-20"),sQuery(id+"F8.wireOp",EDGE,"E106.sketch_text.stroke-21"),sQuery(id+"F8.wireOp",EDGE,"E106.sketch_text.stroke-22"),sQuery(id+"F8.wireOp",EDGE,"E106.sketch_text.stroke-23")])],"isStart":false});
            var Q11;
            Q11=makeQuery(id+"F9.opExtrude","CAP_FACE",FACE,{"disambiguationData":[OSD([sQuery(id+"F8.wireOp",EDGE,"E106.sketch_text.stroke-24"),sQuery(id+"F8.wireOp",EDGE,"E106.sketch_text.stroke-25"),sQuery(id+"F8.wireOp",EDGE,"E106.sketch_text.stroke-26"),sQuery(id+"F8.wireOp",EDGE,"E106.sketch_text.stroke-27"),sQuery(id+"F8.wireOp",EDGE,"E106.sketch_text.stroke-28"),sQuery(id+"F8.wireOp",EDGE,"E106.sketch_text.stroke-29"),sQuery(id+"F8.wireOp",EDGE,"E106.sketch_text.stroke-30"),sQuery(id+"F8.wireOp",EDGE,"E106.sketch_text.stroke-31"),sQuery(id+"F8.wireOp",EDGE,"E106.sketch_text.stroke-32"),sQuery(id+"F8.wireOp",EDGE,"E106.sketch_text.stroke-33")])],"isStart":false});
            var Q12;
            Q12=makeQuery(id+"F9.opExtrude","CAP_FACE",FACE,{"disambiguationData":[OSD([sQuery(id+"F8.wireOp",EDGE,"E106.sketch_text.stroke-34"),sQuery(id+"F8.wireOp",EDGE,"E106.sketch_text.stroke-35"),sQuery(id+"F8.wireOp",EDGE,"E106.sketch_text.stroke-36"),sQuery(id+"F8.wireOp",EDGE,"E106.sketch_text.stroke-37"),sQuery(id+"F8.wireOp",EDGE,"E106.sketch_text.stroke-38"),sQuery(id+"F8.wireOp",EDGE,"E106.sketch_text.stroke-39"),sQuery(id+"F8.wireOp",EDGE,"E106.sketch_text.stroke-40"),sQuery(id+"F8.wireOp",EDGE,"E106.sketch_text.stroke-41"),sQuery(id+"F8.wireOp",EDGE,"E106.sketch_text.stroke-42"),sQuery(id+"F8.wireOp",EDGE,"E106.sketch_text.stroke-43"),sQuery(id+"F8.wireOp",EDGE,"E106.sketch_text.stroke-44"),sQuery(id+"F8.wireOp",EDGE,"E106.sketch_text.stroke-45")])],"isStart":false});
            var Q13;
            Q13=makeQuery(id+"F9.opExtrude","CAP_FACE",FACE,{"disambiguationData":[OSD([sQuery(id+"F8.wireOp",EDGE,"E106.sketch_text.stroke-46"),sQuery(id+"F8.wireOp",EDGE,"E106.sketch_text.stroke-47"),sQuery(id+"F8.wireOp",EDGE,"E106.sketch_text.stroke-48"),sQuery(id+"F8.wireOp",EDGE,"E106.sketch_text.stroke-49"),sQuery(id+"F8.wireOp",EDGE,"E106.sketch_text.stroke-50"),sQuery(id+"F8.wireOp",EDGE,"E106.sketch_text.stroke-51"),sQuery(id+"F8.wireOp",EDGE,"E106.sketch_text.stroke-52"),sQuery(id+"F8.wireOp",EDGE,"E106.sketch_text.stroke-53"),sQuery(id+"F8.wireOp",EDGE,"E106.sketch_text.stroke-54"),sQuery(id+"F8.wireOp",EDGE,"E106.sketch_text.stroke-55"),sQuery(id+"F8.wireOp",EDGE,"E106.sketch_text.stroke-56"),sQuery(id+"F8.wireOp",EDGE,"E106.sketch_text.stroke-57")])],"isStart":false});
            var Q14;
            Q14=makeQuery(id+"F9.opExtrude","SWEPT_EDGE",EDGE,{"disambiguationData":[OSD([sQuery(id+"F8.wireOp",EDGE,"E106.sketch_text.stroke-31"),sQuery(id+"F8.wireOp",EDGE,"E106.sketch_text.stroke-32")])]});
            var Q15;
            Q15=makeQuery(id+"F9.opExtrude","SWEPT_EDGE",EDGE,{"disambiguationData":[OSD([sQuery(id+"F8.wireOp",EDGE,"E106.sketch_text.stroke-21"),sQuery(id+"F8.wireOp",EDGE,"E106.sketch_text.stroke-22")])]});
            fillet(context, id + "F10", {"entities" : qUnion([Q0, Q1, Q2, Q3, Q4, Q5, Q6, Q7, Q8, Q9, Q10, Q11, Q12, Q13, Q14, Q15]), "radius" : 0.38 * mm, "tangentPropagation" : true, "allowEdgeOverflow" : false});
        }
    });
